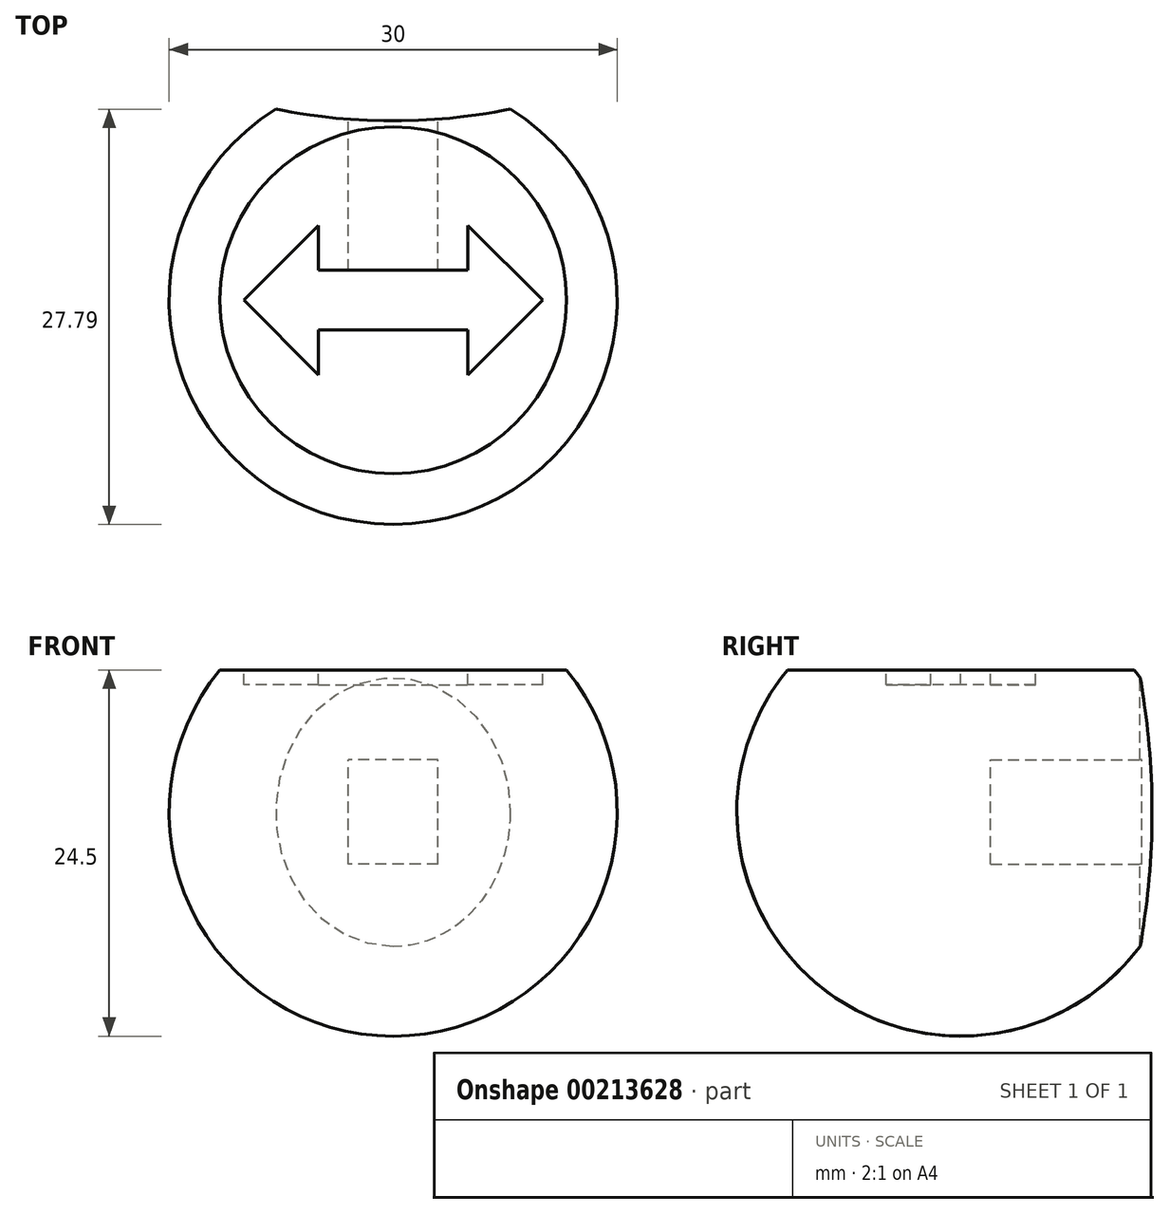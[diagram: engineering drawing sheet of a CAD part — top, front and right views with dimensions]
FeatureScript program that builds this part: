
annotation { "Feature Type Name" : "Feature", "Feature Type Description" : "" }
export const myFeature = defineFeature(function(context is Context, id is Id, definition is map)
    precondition{}
    {
        {
            var Q0;
            Q0=qCreatedBy(makeId("Right.planeOp"),FACE);
            var sketch = newSketch(context, id + "F0", { "sketchPlane" : qUnion([Q0])});
            skLineSegment(sketch, "E0", {"start": v(0, 0) * mm, "end": v(-30, 0) * mm});
            skArc(sketch, "E1", {"start": v(0, 0) * mm, "mid": v(-15, 15) * mm, "end": v(-30, 0) * mm});
            skSolve(sketch);
        }
        {
            var Q0;
            Q0=qSketchRegion(id+"F0",true);
            var Q1;
            Q1=sQuery(id+"F0.wireOp",EDGE,"E0");
            revolve(context, id + "F1", {"entities" : qUnion([Q0]), "axis" : qUnion([Q1]), "revolveType" : RevolveType.FULL});
        }
        {
            var Q0;
            Q0=qCreatedBy(makeId("Top.planeOp"),FACE);
            cPlane(context, id + "F2", {"entities" : qUnion([Q0]), "cplaneType" : CPlaneType.OFFSET, "offset" : 15 * mm, "width" : 150 * mm, "height" : 150 * mm});
        }
        {
            var Q0;
            Q0=qCreatedBy(id+"F2.planeOp",FACE);
            var sketch = newSketch(context, id + "F3", { "sketchPlane" : qUnion([Q0])});
            skLineSegment(sketch, "E2", {"start": v(0, 0) * mm, "end": v(0, -16.03) * mm, "construction": true});
            skLineSegment(sketch, "E3", {"start": v(0, 0) * mm, "end": v(-15, 0) * mm});
            skLineSegment(sketch, "E4", {"start": v(0, 0) * mm, "end": v(15, 0) * mm});
            skArc(sketch, "E5", {"start": v(-15, 0) * mm, "mid": v(0, -3) * mm, "end": v(15, 0) * mm});
            skSolve(sketch);
        }
        {
            var Q0;
            Q0=qSketchRegion(id+"F3",true);
            extrude(context, id + "F4", {"entities" : qUnion([Q0]), "operationType" : NewBodyOperationType.REMOVE, "endBound" : BoundingType.THROUGH_ALL, "oppositeDirection" : true, "depth" : 25 * mm});
        }
        {
            var Q0;
            Q0=qCreatedBy(makeId("Front.planeOp"),FACE);
            var sketch = newSketch(context, id + "F5", { "sketchPlane" : qUnion([Q0])});
            skLineSegment(sketch, "E6.bottom", {"start": v(3, -3.5) * mm, "end": v(-3, -3.5) * mm});
            skLineSegment(sketch, "E6.top", {"start": v(3, 3.5) * mm, "end": v(-3, 3.5) * mm});
            skLineSegment(sketch, "E6.left", {"start": v(3, -3.5) * mm, "end": v(3, 3.5) * mm});
            skLineSegment(sketch, "E6.right", {"start": v(-3, -3.5) * mm, "end": v(-3, 3.5) * mm});
            skPoint(sketch, "E6.middle", {"position": v(0, 0) * mm});
            skSolve(sketch);
        }
        {
            var Q0;
            Q0=qSketchRegion(id+"F5",true);
            extrude(context, id + "F6", {"entities" : qUnion([Q0]), "operationType" : NewBodyOperationType.REMOVE, "depth" : 13 * mm});
        }
        {
            var Q0;
            Q0=qCreatedBy(makeId("Front.planeOp"),FACE);
            var sketch = newSketch(context, id + "F7", { "sketchPlane" : qUnion([Q0])});
            skLineSegment(sketch, "E7", {"start": v(23.47, 9.5) * mm, "end": v(-26.93, 9.5) * mm});
            skLineSegment(sketch, "E8", {"start": v(23.47, 9.5) * mm, "end": v(23.47, 17.53) * mm});
            skLineSegment(sketch, "E9", {"start": v(23.47, 17.53) * mm, "end": v(-26.93, 17.53) * mm});
            skLineSegment(sketch, "E10", {"start": v(-26.93, 17.53) * mm, "end": v(-26.93, 9.5) * mm});
            skSolve(sketch);
        }
        {
            var Q0;
            Q0=qSketchRegion(id+"F7",true);
            extrude(context, id + "F8", {"entities" : qUnion([Q0]), "operationType" : NewBodyOperationType.REMOVE, "endBound" : BoundingType.THROUGH_ALL, "depth" : 25 * mm});
        }
        {
            var Q0;
            Q0=makeQuery(id+"F8.boolean.opBoolean","COPY",FACE,{"derivedFrom":makeQuery(id+"F8.opExtrude","SWEPT_FACE",FACE,{"disambiguationData":[OSD([sQuery(id+"F7.wireOp",EDGE,"E7")])]})});
            var sketch = newSketch(context, id + "F9", { "sketchPlane" : qUnion([Q0])});
            skLineSegment(sketch, "E11", {"start": v(0, -15) * mm, "end": v(-11.6, -15) * mm, "construction": true});
            skLineSegment(sketch, "E12", {"start": v(0, -15) * mm, "end": v(11.6, -15) * mm, "construction": true});
            skLineSegment(sketch, "E13.bottom", {"start": v(-5, -13) * mm, "end": v(5, -13) * mm});
            skLineSegment(sketch, "E13.top", {"start": v(-5, -17) * mm, "end": v(5, -17) * mm});
            skLineSegment(sketch, "E13.left", {"start": v(-5, -13) * mm, "end": v(-5, -17) * mm});
            skLineSegment(sketch, "E13.right", {"start": v(5, -13) * mm, "end": v(5, -17) * mm});
            skPoint(sketch, "E13.middle", {"position": v(0, -15) * mm});
            skLineSegment(sketch, "E14", {"start": v(5, -13) * mm, "end": v(5, -10) * mm});
            skLineSegment(sketch, "E15", {"start": v(5, -10) * mm, "end": v(10, -15) * mm});
            skLineSegment(sketch, "E16", {"start": v(10, -15) * mm, "end": v(5, -20) * mm});
            skLineSegment(sketch, "E17", {"start": v(5, -20) * mm, "end": v(5, -17) * mm});
            skLineSegment(sketch, "E18", {"start": v(0, -17) * mm, "end": v(0, -13) * mm, "construction": true});
            skLineSegment(sketch, "E19.MirrorCS", {"start": v(-5, -13) * mm, "end": v(-5, -10) * mm});
            skLineSegment(sketch, "E20.MirrorCS", {"start": v(-5, -10) * mm, "end": v(-10, -15) * mm});
            skLineSegment(sketch, "E21.MirrorCS", {"start": v(-10, -15) * mm, "end": v(-5, -20) * mm});
            skLineSegment(sketch, "E22.MirrorCS", {"start": v(-5, -20) * mm, "end": v(-5, -17) * mm});
            skSolve(sketch);
        }
        {
            var Q0;
            Q0=qSketchRegion(id+"F9",true);
            extrude(context, id + "F10", {"entities" : qUnion([Q0]), "operationType" : NewBodyOperationType.REMOVE, "oppositeDirection" : true, "depth" : 1 * mm});
        }
    });
